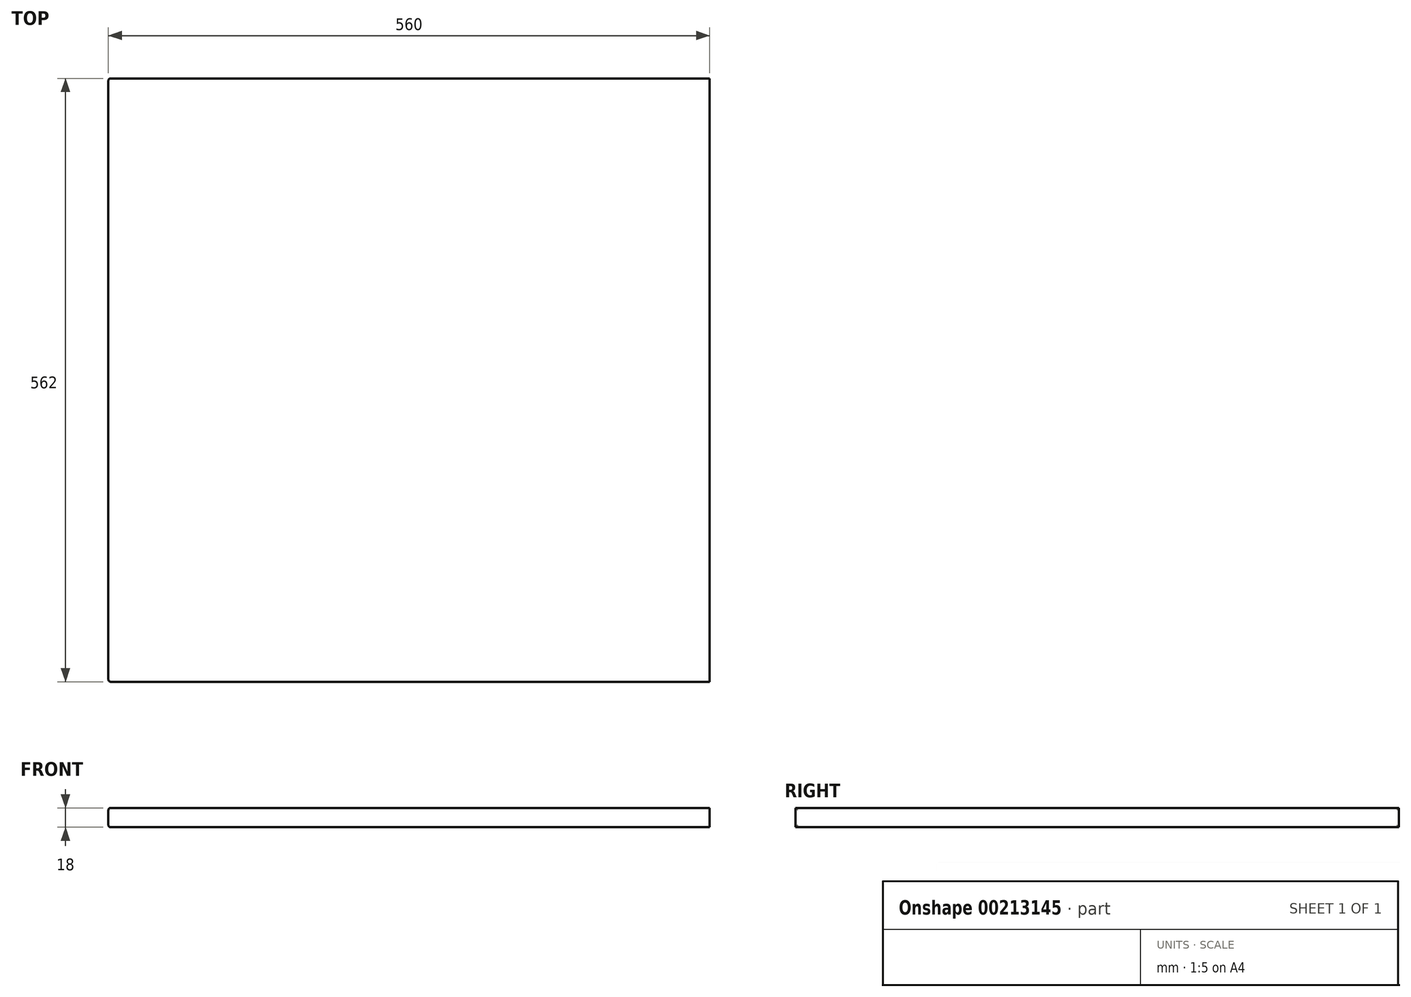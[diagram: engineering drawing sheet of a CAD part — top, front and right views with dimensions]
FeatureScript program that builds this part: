
annotation { "Feature Type Name" : "Feature", "Feature Type Description" : "" }
export const myFeature = defineFeature(function(context is Context, id is Id, definition is map)
    precondition{}
    {
        {
            var Q0;
            Q0=qCreatedBy(makeId("Top.planeOp"),FACE);
            var sketch = newSketch(context, id + "F0", { "sketchPlane" : qUnion([Q0])});
            skLineSegment(sketch, "E0.bottom", {"start": v(280, 281) * mm, "end": v(-280, 281) * mm});
            skLineSegment(sketch, "E0.top", {"start": v(280, -281) * mm, "end": v(-280, -281) * mm});
            skLineSegment(sketch, "E0.left", {"start": v(280, 281) * mm, "end": v(280, -281) * mm});
            skLineSegment(sketch, "E0.right", {"start": v(-280, 281) * mm, "end": v(-280, -281) * mm});
            skPoint(sketch, "E0.middle", {"position": v(0, 0) * mm});
            skSolve(sketch);
        }
        {
            var Q0;
            Q0=makeQuery(id+"F0.imprint","IMPRINT",FACE,{"disambiguationData":[TD([[makeQuery(id+"F0.imprint","IMPRINT",EDGE,{"derivedFrom":sQuery(id+"F0.wireOp",EDGE,"E0.bottom")}),1.0]])]});
            extrude(context, id + "F1", {"entities" : qUnion([Q0]), "endBound" : BoundingType.SYMMETRIC, "depth" : 18 * mm});
        }
        {
            var Q0;
            Q0=makeQuery(id+"F1.opExtrude","SWEPT_FACE",FACE,{"disambiguationData":[OSD([sQuery(id+"F0.wireOp",EDGE,"E0.right")])]});
            fillet(context, id + "F2", {"entities" : qUnion([Q0]), "radius" : 2 * mm, "tangentPropagation" : true, "allowEdgeOverflow" : false});
        }
    });
